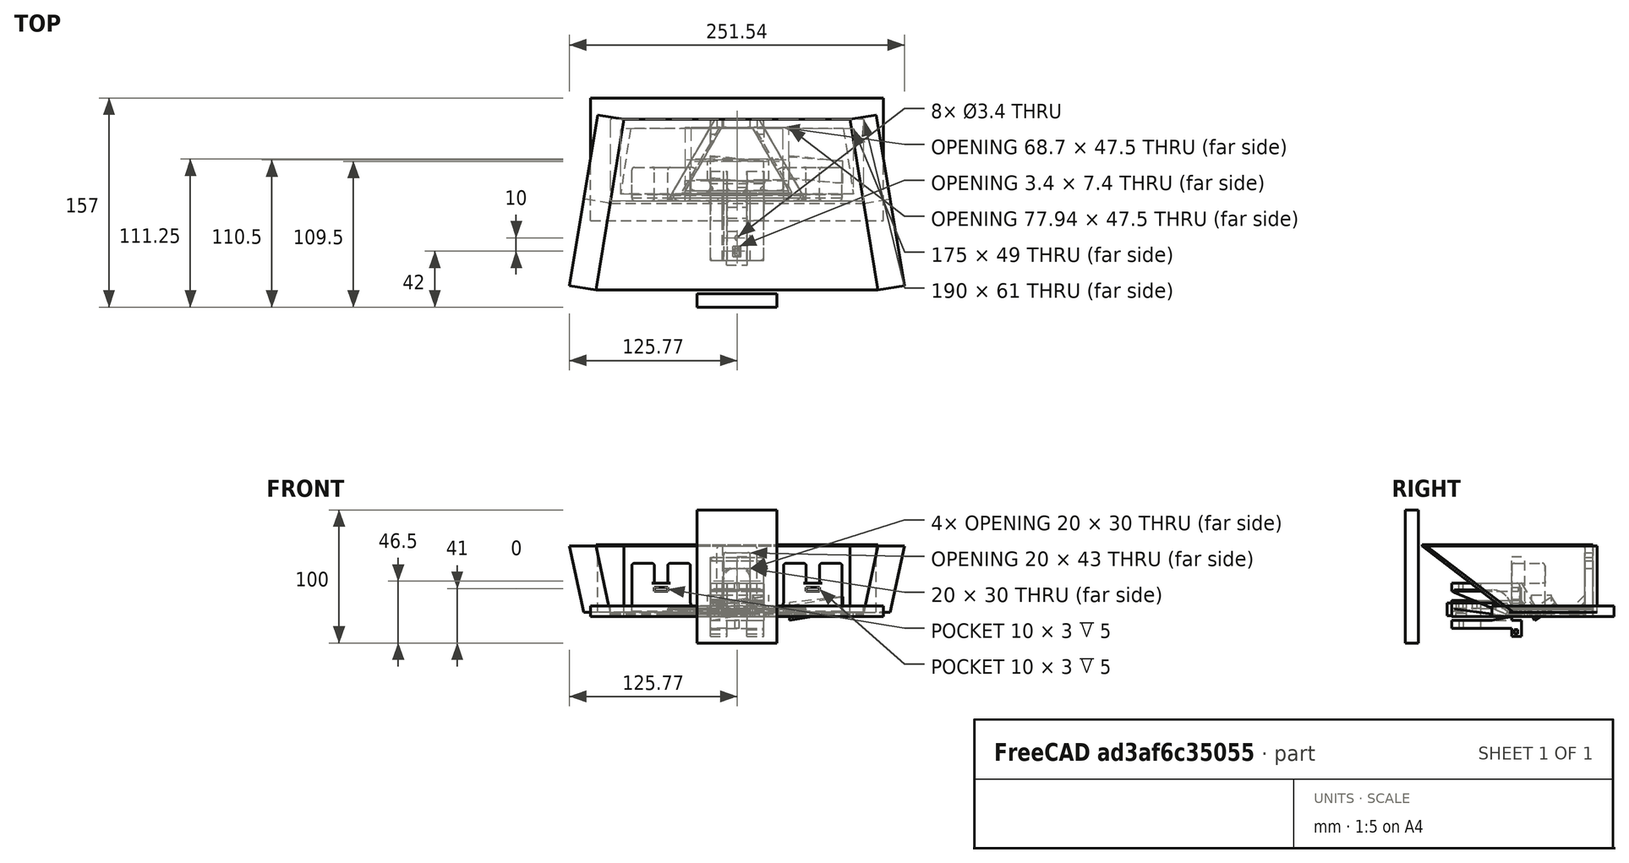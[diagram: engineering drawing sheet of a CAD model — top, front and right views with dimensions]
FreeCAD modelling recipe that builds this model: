
FCSTD DOCUMENT  (FreeCAD 1.0R39319 (Git))
Label: soporte_celular_auto_2bloques
License: All rights reserved
LicenseURL: http://en.wikipedia.org/wiki/All_rights_reserved
objects: Part::Box×64, Part::Cut×50, Part::Fillet×29, Part::Extrusion×19, Sketcher::SketchObject×18, Part::MultiFuse×16, Part::Feature×12, Part::Prism×6, Part::Cylinder×5, Part::Chamfer×2, Mesh::Feature×1
note: 239 computed .brp shape members not serialized (recipe doc carries the construction recipe); baked Part::Feature solids carry a one-line shape summary decoded from their .brp

FEATURE [Sketcher::SketchObject] Sketch001
  ArcFitTolerance = 0
  FullyConstrained = true
  MakeInternals = false
  sketch-geometry (4):
    g0: LineSegment StartX=-95 StartY=0 StartZ=0 EndX=95 EndY=-9e-16 EndZ=0
    g1: LineSegment StartX=-95 StartY=0 StartZ=0 EndX=-85 EndY=61 EndZ=0
    g2: LineSegment StartX=95 StartY=-9e-16 StartZ=0 EndX=85 EndY=61 EndZ=0
    g3: LineSegment StartX=-85 StartY=61 StartZ=0 EndX=85 EndY=61 EndZ=0
  constraints (10):
    c: PointOnObject(g0,g-1)
    c: Symmetric(g0,g0,g-2)
    c: DistanceX(g0,g0) = 190
    c: Coincident(g1,g0)
    c: Coincident(g2,g0)
    c: Coincident(g3,g1)
    c: Coincident(g3,g2)
    c: Symmetric(g1,g2,g-2)
    c: DistanceX(g3,g3) = 170
    c: DistanceY(g0,g2) = 61
FEATURE [Part::Extrusion] Extrude
  Base = -> Sketch001
  Dir = (0,0,1)
  DirMode = 2
  FaceMakerClass = Part::FaceMakerBullseye
  FaceMakerMode = 3
  LengthFwd = 10
  LengthRev = 0
  Solid = true
  Symmetric = false
FEATURE [Part::Box] Box  label="Cube"
  AttacherType = Attacher::AttachEngine3D
  Height = 8
  Length = 220
  Placement = pos=(-110,-15,0) rot=(0,0,1;0rad)
  Width = 92
FEATURE [Part::Cut] Cut  label="molde_cortador"
  Base = -> Box
  Tool = -> Extrude
FEATURE [Part::Prism] Prism002
  AttacherType = Attacher::AttachEngine3D
  Circumradius = 60
  FirstAngle = 0
  Height = 6
  Placement = pos=(0,23,0) rot=(0,0,-1;0.523599rad)
  Polygon = 3
  SecondAngle = 0
FEATURE [Part::Prism] Prism003
  AttacherType = Attacher::AttachEngine3D
  Circumradius = 45
  FirstAngle = 0
  Height = 6
  Placement = pos=(0,23,0) rot=(0,0,-1;0.523599rad)
  Polygon = 3
  SecondAngle = 0
FEATURE [Part::Cut] Cut001
  Base = -> Prism002
  Placement = pos=(0,7,0) rot=(0,0,1;0rad)
  Tool = -> Prism003
FEATURE [Part::Box] Box001  label="Cube001"
  AttacherType = Attacher::AttachEngine3D
  Height = 6
  Length = 32
  Placement = pos=(-16,55,0) rot=(0,0,1;0rad)
  Width = 6
FEATURE [Part::MultiFuse] Fusion
  Shapes = -> [Cut001,Box001]
FEATURE [Sketcher::SketchObject] Sketch002
  ArcFitTolerance = 0
  FullyConstrained = true
  MakeInternals = false
  sketch-geometry (4):
    g0: LineSegment StartX=-95 StartY=0 StartZ=0 EndX=95 EndY=-9e-16 EndZ=0
    g1: LineSegment StartX=-95 StartY=0 StartZ=0 EndX=-85 EndY=61 EndZ=0
    g2: LineSegment StartX=95 StartY=-9e-16 StartZ=0 EndX=85 EndY=61 EndZ=0
    g3: LineSegment StartX=-85 StartY=61 StartZ=0 EndX=85 EndY=61 EndZ=0
  constraints (10):
    c: PointOnObject(g0,g-1)
    c: Symmetric(g0,g0,g-2)
    c: DistanceX(g0,g0) = 190
    c: Coincident(g1,g0)
    c: Coincident(g2,g0)
    c: Coincident(g3,g1)
    c: Coincident(g3,g2)
    c: Symmetric(g1,g2,g-2)
    c: DistanceX(g3,g3) = 170
    c: DistanceY(g0,g2) = 61
FEATURE [Part::Box] Box002  label="Cube002"
  AttacherType = Attacher::AttachEngine3D
  Height = 8
  Length = 220
  Placement = pos=(-110,-15,0) rot=(0,0,1;0rad)
  Width = 113
FEATURE [Part::Extrusion] Extrude001
  Base = -> Sketch002
  Dir = (0,0,1)
  DirMode = 2
  FaceMakerClass = Part::FaceMakerBullseye
  FaceMakerMode = 3
  LengthFwd = 10
  LengthRev = 0
  Solid = true
  Symmetric = false
FEATURE [Part::Cut] Cut002  label="molde_cortador001"
  Base = -> Box002
  Tool = -> Extrude001
FEATURE [Part::Cut] Cut003  label="base_triangulo"
  Base = -> Fusion
  Tool = -> Cut002
FEATURE [Part::Box] Box003  label="Cube003"
  AttacherType = Attacher::AttachEngine3D
  Height = 3
  Length = 220
  Placement = pos=(-110,2,0) rot=(0,0,1;0rad)
  Width = 2.5
FEATURE [Part::Cut] Cut004  label="base_triangulo_con_canaleta"
  Base = -> Cut003
  Tool = -> Box003
FEATURE [Part::Feature] Fusion001
  shape: bbox 190 x 63 x 3 mm, 10 faces (baked)
FEATURE [Sketcher::SketchObject] Sketch003
  ArcFitTolerance = 0
  ExternalGeometry = -> [Fusion001]
  FullyConstrained = true
  MakeInternals = false
  sketch-geometry (4):
    g0: LineSegment StartX=-87.5 StartY=0 StartZ=0 EndX=87.5 EndY=0 EndZ=0
    g1: LineSegment StartX=-87.5 StartY=0 StartZ=0 EndX=-80 EndY=49 EndZ=0
    g2: LineSegment StartX=87.5 StartY=0 StartZ=0 EndX=80 EndY=49 EndZ=0
    g3: LineSegment StartX=-80 StartY=49 StartZ=0 EndX=80 EndY=49 EndZ=0
  constraints (10):
    c: PointOnObject(g0,g-1)
    c: Symmetric(g0,g0,g-2)
    c: DistanceX(g0,g0) = 175
    c: Coincident(g1,g0)
    c: Coincident(g2,g0)
    c: Coincident(g3,g1)
    c: Coincident(g3,g2)
    c: Symmetric(g1,g2,g-2)
    c: DistanceX(g3,g3) = 160
    c: DistanceY(g0,g2) = 49
FEATURE [Part::Extrusion] Extrude002
  Base = -> Sketch003
  Dir = (0,0,1)
  DirMode = 2
  FaceMakerClass = Part::FaceMakerBullseye
  FaceMakerMode = 3
  LengthFwd = 10
  LengthRev = 0
  Placement = pos=(0,5,0) rot=(0,0,1;0rad)
  Solid = true
  Symmetric = false
FEATURE [Part::Cut] Cut004002  label="base"
  Base = -> Fusion001
  Tool = -> Extrude002
FEATURE [Sketcher::SketchObject] Sketch004
  ArcFitTolerance = 0
  AttachmentSupport = -> [Cut004002]
  ExternalGeometry = -> [Cut004002]
  FullyConstrained = true
  MakeInternals = false
  MapMode = 5
  Placement = pos=(-92.5137,15.1662,-3.7e-15) rot=(-0.51489,0.606172,0.606172;4.09257rad)
  sketch-geometry (4):
    g0: LineSegment StartX=-46.4456 StartY=3 StartZ=0 EndX=17.3423 EndY=3 EndZ=0
    g1: LineSegment StartX=-46.4456 StartY=3 StartZ=0 EndX=-46.4456 EndY=53 EndZ=0
    g2: LineSegment StartX=-46.4456 StartY=53 StartZ=0 EndX=83.5544 EndY=53 EndZ=0
    g3: LineSegment StartX=83.5544 StartY=53 StartZ=0 EndX=17.3423 EndY=3 EndZ=0
  constraints (10):
    c: Coincident(g0,g-4)
    c: Coincident(g0,g-3)
    c: Vertical(g1)
    c: Coincident(g0,g1)
    c: DistanceY(g1,g1) = 50
    c: Coincident(g2,g1)
    c: Horizontal(g2)
    c: DistanceX(g2,g2) = 130
    c: Coincident(g3,g2)
    c: Coincident(g3,g0)
FEATURE [Part::Feature] Fusion002
  shape: bbox 190 x 63 x 3 mm, 10 faces (baked)
FEATURE [Sketcher::SketchObject] Sketch005
  ArcFitTolerance = 0
  ExternalGeometry = -> [Fusion002]
  FullyConstrained = true
  MakeInternals = false
  sketch-geometry (4):
    g0: LineSegment StartX=-87.5 StartY=0 StartZ=0 EndX=87.5 EndY=0 EndZ=0
    g1: LineSegment StartX=-87.5 StartY=0 StartZ=0 EndX=-80 EndY=49 EndZ=0
    g2: LineSegment StartX=87.5 StartY=0 StartZ=0 EndX=80 EndY=49 EndZ=0
    g3: LineSegment StartX=-80 StartY=49 StartZ=0 EndX=80 EndY=49 EndZ=0
  constraints (10):
    c: PointOnObject(g0,g-1)
    c: Symmetric(g0,g0,g-2)
    c: DistanceX(g0,g0) = 175
    c: Coincident(g1,g0)
    c: Coincident(g2,g0)
    c: Coincident(g3,g1)
    c: Coincident(g3,g2)
    c: Symmetric(g1,g2,g-2)
    c: DistanceX(g3,g3) = 160
    c: DistanceY(g0,g2) = 49
FEATURE [Part::Extrusion] Extrude003
  Base = -> Sketch005
  Dir = (0,0,1)
  DirMode = 2
  FaceMakerClass = Part::FaceMakerBullseye
  FaceMakerMode = 3
  LengthFwd = 10
  LengthRev = 0
  Placement = pos=(0,5,0) rot=(0,0,1;0rad)
  Solid = true
  Symmetric = false
FEATURE [Part::Cut] Cut004003  label="base001"
  Base = -> Fusion002
  Tool = -> Extrude003
FEATURE [Sketcher::SketchObject] Sketch006
  ArcFitTolerance = 0
  AttachmentSupport = -> [Cut004003]
  ExternalGeometry = -> [Cut004003]
  FullyConstrained = true
  MakeInternals = false
  MapMode = 5
  Placement = pos=(92.5137,15.1662,-2.34e-14) rot=(0.51489,0.606172,0.606172;2.19062rad)
  sketch-geometry (4):
    g0: LineSegment StartX=-17.3423 StartY=3 StartZ=0 EndX=46.4456 EndY=3 EndZ=0
    g1: LineSegment StartX=46.4456 StartY=3 StartZ=0 EndX=46.4456 EndY=53 EndZ=0
    g2: LineSegment StartX=46.4456 StartY=53 StartZ=0 EndX=-83.5544 EndY=53 EndZ=0
    g3: LineSegment StartX=-83.5544 StartY=53 StartZ=0 EndX=-17.3423 EndY=3 EndZ=0
  constraints (10):
    c: Coincident(g0,g-4)
    c: Coincident(g0,g-3)
    c: Coincident(g1,g0)
    c: Vertical(g1)
    c: DistanceY(g1,g1) = 50
    c: Coincident(g2,g1)
    c: Horizontal(g2)
    c: Coincident(g3,g2)
    c: DistanceX(g2,g2) = 130
    c: Coincident(g0,g3)
FEATURE [Part::Extrusion] Extrude004
  Base = -> Sketch006
  Dir = (0.986828,0.161775,1e-16)
  DirMode = 2
  FaceMakerClass = Part::FaceMakerBullseye
  FaceMakerMode = 3
  LengthFwd = 20
  LengthRev = 0
  Solid = true
  Symmetric = false
FEATURE [Part::Extrusion] Extrude006
  Base = -> Sketch004
  Dir = (-0.986828,0.161775,1e-16)
  DirMode = 2
  FaceMakerClass = Part::FaceMakerBullseye
  FaceMakerMode = 3
  LengthFwd = 20
  LengthRev = 0
  Solid = true
  Symmetric = false
FEATURE [Sketcher::SketchObject] Sketch
  ArcFitTolerance = 0
  ExternalGeometry = -> [Extrude006,Extrude004]
  FullyConstrained = true
  MakeInternals = false
  sketch-geometry (4):
    g0: LineSegment StartX=-85 StartY=61 StartZ=0 EndX=85 EndY=61 EndZ=0
    g1: LineSegment StartX=-106.031 StartY=-67.2876 StartZ=0 EndX=106.031 EndY=-67.2876 EndZ=0
    g2: LineSegment StartX=-85 StartY=61 StartZ=0 EndX=-106.031 EndY=-67.2876 EndZ=0
    g3: LineSegment StartX=85 StartY=61 StartZ=0 EndX=106.031 EndY=-67.2876 EndZ=0
  constraints (8):
    c: Coincident(g0,g-3)
    c: Coincident(g0,g-4)
    c: Coincident(g1,g-3)
    c: Coincident(g1,g-4)
    c: Coincident(g0,g2)
    c: Coincident(g0,g3)
    c: Coincident(g1,g2)
    c: Coincident(g1,g3)
FEATURE [Part::Extrusion] Extrude007  label="techo_posicion"
  Base = -> Sketch
  Dir = (0,0,1)
  DirMode = 2
  FaceMakerClass = Part::FaceMakerBullseye
  FaceMakerMode = 3
  LengthFwd = 1
  LengthRev = 0
  Placement = pos=(0,0,53) rot=(0,0,1;0rad)
  Solid = true
  Symmetric = false
FEATURE [Part::Box] Box004  label="Cube004"
  AttacherType = Attacher::AttachEngine3D
  Height = 44.5
  Length = 40
  Placement = pos=(-20,55,0) rot=(0,0,1;0rad)
  Width = 6
FEATURE [Part::Box] Box005  label="Cube005"
  AttacherType = Attacher::AttachEngine3D
  Height = 30
  Length = 20
  Placement = pos=(-10,55,6) rot=(0,0,1;0rad)
  Width = 6
FEATURE [Part::Cut] Cut004004  label="parte_trasera"
  Base = -> Box004
  Tool = -> Box005
FEATURE [Part::Box] Box006  label="Cube006"
  AttacherType = Attacher::AttachEngine3D
  Height = 6
  Length = 40
  Placement = pos=(0,0,20) rot=(0,0,1;0rad)
  Width = 51
FEATURE [Part::Box] Box007  label="Cube007"
  AttacherType = Attacher::AttachEngine3D
  Height = 6
  Length = 15
  Placement = pos=(12.5,22,20) rot=(0,0,1;0rad)
  Width = 70
FEATURE [Part::Cut] Cut004005
  Base = -> Box006
  Placement = pos=(-20,0,-1) rot=(0,0,1;0rad)
  Tool = -> Box007
FEATURE [Part::Cylinder] Cylinder
  Angle = 360
  AttacherType = Attacher::AttachEngine3D
  FirstAngle = 0
  Height = 30
  Placement = pos=(0,7,0) rot=(0,0,1;0rad)
  Radius = 1.7
  SecondAngle = 0
FEATURE [Part::Cut] Cut004006
  Base = -> Cut004005
  Placement = pos=(0,-45,0) rot=(0,0,1;0rad)
  Tool = -> Cylinder
FEATURE [Part::Box] Box008  label="celular"
  AttacherType = Attacher::AttachEngine3D
  Height = 100
  Length = 60
  Placement = pos=(-30,-80,-20) rot=(0,0,1;0rad)
  Width = 10
FEATURE [Part::Box] Box009  label="Cube008"
  AttacherType = Attacher::AttachEngine3D
  Height = 12
  Length = 12.5
  Placement = pos=(7.5,0,13) rot=(0,0,1;0rad)
  Width = 7.5
FEATURE [Part::Box] Box010  label="Cube009"
  AttacherType = Attacher::AttachEngine3D
  Height = 12
  Length = 12.5
  Placement = pos=(-20,0,13) rot=(0,0,1;0rad)
  Width = 7.5
FEATURE [Part::Feature] Fusion004001  label="Fusion005"
  shape: bbox 99.53 x 106 x 53 mm, 44 faces (baked)
FEATURE [Part::Fillet] Fillet006
  Base = -> Fusion004001
  EdgeLinks = -> Fusion004001 [Edge75,Edge79]
  Edges = 2 edges r=15: [Edge75,Edge79]
FEATURE [Part::Fillet] Fillet007
  Base = -> Fillet006
  EdgeLinks = -> Fillet006 [Edge65,Edge67]
  Edges = 2 edges r=2: [Edge65,Edge67]
FEATURE [Part::Fillet] Fillet008  label="soporte_final_v2.1_00"
  Base = -> Fillet007
  EdgeLinks = -> Fillet007 [Edge3,Edge19]
  Edges = 2 edges r=2: [Edge3,Edge19]
FEATURE [Part::Feature] Fillet008001  label="soporte_final_v2.002"
  shape: bbox 99.53 x 106 x 53 mm, 50 faces (baked)
FEATURE [Part::Box] Box011  label="Cube010"
  AttacherType = Attacher::AttachEngine3D
  Height = 100
  Length = 70
  Placement = pos=(10,-51,0) rot=(0,0,1;0rad)
  Width = 120
FEATURE [Part::Cut] Cut004007
  Base = -> Fillet008001
  Tool = -> Box011
FEATURE [Part::Box] Box012  label="Cube011"
  AttacherType = Attacher::AttachEngine3D
  Height = 100
  Length = 70
  Placement = pos=(-11,13,0) rot=(0,0,1;0rad)
  Width = 120
FEATURE [Part::Cut] Cut004008
  Base = -> Cut004007
  Tool = -> Box012
FEATURE [Part::Box] Box013  label="Cube012"
  AttacherType = Attacher::AttachEngine3D
  Height = 10
  Length = 40
  Placement = pos=(-60,0,2) rot=(0,0,1;0rad)
  Width = 70
FEATURE [Part::Cut] Cut004009
  Base = -> Cut004008
  Tool = -> Box013
FEATURE [Part::Box] Box014  label="Cube013"
  AttacherType = Attacher::AttachEngine3D
  Height = 50
  Length = 19
  Placement = pos=(-30,-60,0) rot=(0,0,1;0rad)
  Width = 60
FEATURE [Part::Cut] Cut004010
  Base = -> Cut004009
  Tool = -> Box014
FEATURE [Part::Box] Box015  label="Cube014"
  AttacherType = Attacher::AttachEngine3D
  Height = 30
  Length = 10
  Placement = pos=(-21,0,2) rot=(0,0,1;0rad)
  Width = 10
FEATURE [Part::Cut] Cut004011
  Base = -> Cut004010
  Tool = -> Box015
FEATURE [Part::Fillet] Fillet008002  label="soporte_final_v2.1"
  Base = -> Fillet008
  EdgeLinks = -> Fillet008 [Edge7,Edge53,Edge58,Edge60]
  Edges = 4 edges r=3: [Edge7,Edge53,Edge58,Edge60]
FEATURE [Part::Box] Box016  label="Cube015"
  AttacherType = Attacher::AttachEngine3D
  Height = 10
  Length = 40
  Placement = pos=(-54,-7,0) rot=(0,0,1;0rad)
  Width = 10
FEATURE [Part::Cut] Cut004012  label="test"
  Base = -> Cut004011
  Tool = -> Box016
FEATURE [Part::MultiFuse] Fusion004002  label="pieza_fronta_cuadrada_sin_soportes"
  Placement = pos=(0,0,-15) rot=(0,0,1;0rad)
  Shapes = -> [Cut004006,Box009,Box010]
FEATURE [Part::Box] Box017  label="Cube016"
  AttacherType = Attacher::AttachEngine3D
  Height = 22
  Length = 12.5
  Placement = pos=(7.5,0,3) rot=(0,0,1;0rad)
  Width = 7.5
FEATURE [Part::Cylinder] Cylinder001
  Angle = 360
  AttacherType = Attacher::AttachEngine3D
  FirstAngle = 0
  Height = 30
  Placement = pos=(0,7,0) rot=(0,0,1;0rad)
  Radius = 1.7
  SecondAngle = 0
FEATURE [Part::Box] Box018  label="Cube017"
  AttacherType = Attacher::AttachEngine3D
  Height = 6
  Length = 40
  Placement = pos=(0,0,20) rot=(0,0,1;0rad)
  Width = 51
FEATURE [Part::Box] Box019  label="Cube018"
  AttacherType = Attacher::AttachEngine3D
  Height = 6
  Length = 15
  Placement = pos=(12.5,22,20) rot=(0,0,1;0rad)
  Width = 70
FEATURE [Part::Cut] Cut004013
  Base = -> Box018
  Placement = pos=(-20,0,-1) rot=(0,0,1;0rad)
  Tool = -> Box019
FEATURE [Part::Cut] Cut004014
  Base = -> Cut004013
  Placement = pos=(0,-45,0) rot=(0,0,1;0rad)
  Tool = -> Cylinder001
FEATURE [Part::Box] Box020  label="Cube019"
  AttacherType = Attacher::AttachEngine3D
  Height = 22
  Length = 12.5
  Placement = pos=(-20,0,3) rot=(0,0,1;0rad)
  Width = 7.5
FEATURE [Part::MultiFuse] Fusion004004
  Shapes = -> [Cut004014,Box017,Box020]
FEATURE [Sketcher::SketchObject] Sketch009
  ArcFitTolerance = 0
  FullyConstrained = true
  MakeInternals = false
  sketch-geometry (4):
    g0: LineSegment StartX=-95 StartY=0 StartZ=0 EndX=95 EndY=-9e-16 EndZ=0
    g1: LineSegment StartX=-95 StartY=0 StartZ=0 EndX=-85 EndY=61 EndZ=0
    g2: LineSegment StartX=95 StartY=-9e-16 StartZ=0 EndX=85 EndY=61 EndZ=0
    g3: LineSegment StartX=-85 StartY=61 StartZ=0 EndX=85 EndY=61 EndZ=0
  constraints (10):
    c: PointOnObject(g0,g-1)
    c: Symmetric(g0,g0,g-2)
    c: DistanceX(g0,g0) = 190
    c: Coincident(g1,g0)
    c: Coincident(g2,g0)
    c: Coincident(g3,g1)
    c: Coincident(g3,g2)
    c: Symmetric(g1,g2,g-2)
    c: DistanceX(g3,g3) = 170
    c: DistanceY(g0,g2) = 61
FEATURE [Part::Extrusion] Extrude011
  Base = -> Sketch009
  Dir = (0,0,1)
  DirMode = 2
  FaceMakerClass = Part::FaceMakerBullseye
  FaceMakerMode = 3
  LengthFwd = 10
  LengthRev = 0
  Solid = true
  Symmetric = false
FEATURE [Part::Prism] Prism004
  AttacherType = Attacher::AttachEngine3D
  Circumradius = 45
  FirstAngle = 0
  Height = 6
  Placement = pos=(0,23,0) rot=(0,0,-1;0.523599rad)
  Polygon = 3
  SecondAngle = 0
FEATURE [Part::Box] Box023  label="corte_canaleta"
  AttacherType = Attacher::AttachEngine3D
  Height = 3
  Length = 220
  Placement = pos=(-110,2,0) rot=(0,0,1;0rad)
  Width = 2.5
FEATURE [Part::Box] Box024  label="Cube023"
  AttacherType = Attacher::AttachEngine3D
  Height = 8
  Length = 220
  Placement = pos=(-110,-15,0) rot=(0,0,1;0rad)
  Width = 113
FEATURE [Part::Cut] Cut004020  label="molde_cortador002"
  Base = -> Box024
  Tool = -> Extrude011
FEATURE [Part::Prism] Prism005
  AttacherType = Attacher::AttachEngine3D
  Circumradius = 60
  FirstAngle = 0
  Height = 6
  Placement = pos=(0,23,0) rot=(0,0,-1;0.523599rad)
  Polygon = 3
  SecondAngle = 0
FEATURE [Part::Cut] Cut004019
  Base = -> Prism005
  Placement = pos=(0,7,0) rot=(0,0,1;0rad)
  Tool = -> Prism004
FEATURE [Part::Box] Box026  label="Cube025"
  AttacherType = Attacher::AttachEngine3D
  Height = 6
  Length = 32
  Placement = pos=(-16,55,0) rot=(0,0,1;0rad)
  Width = 6
FEATURE [Part::MultiFuse] Fusion004005
  Shapes = -> [Cut004019,Box026]
FEATURE [Part::Cut] Cut004015  label="base_triangulo001"
  Base = -> Fusion004005
  Tool = -> Cut004020
FEATURE [Part::Cut] Cut004016  label="base_triangulo_con_canaleta001"
  Base = -> Cut004015
  Tool = -> Box023
FEATURE [Part::Feature] Fusion004009001  label="pieza_sin_refinar001"
  shape: bbox 103.9 x 106 x 42 mm, 40 faces (baked)
FEATURE [Part::Fillet] Fillet
  Base = -> Fusion004009001
  EdgeLinks = -> Fusion004009001 [Edge4,Edge8,Edge38,Edge44,Edge56,Edge57,Edge60,Edge62,Edge64,Edge66,Edge67,Edge68]
  Edges = 12 edges r=2: [Edge4,Edge8,Edge38,Edge44,Edge56,Edge57,Edge60,Edge62,Edge64,Edge66,Edge67,Edge68]
FEATURE [Part::Fillet] Fillet008003
  Base = -> Fillet
  EdgeLinks = -> Fillet [Edge92,Edge98]
  Edges = 2 edges r=2: [Edge92,Edge98]
FEATURE [Part::Fillet] Fillet008004
  Base = -> Fillet008003
  EdgeLinks = -> Fillet008003 [Edge22,Edge28,Edge83,Edge88]
  Edges = 4 edges r=2: [Edge22,Edge28,Edge83,Edge88]
FEATURE [Part::Fillet] Fillet008005
  Base = -> Fillet008004
  EdgeLinks = -> Fillet008004 [Edge105,Edge107,Edge108,Edge111]
  Edges = 4 edges r=5: [Edge105,Edge107,Edge108,Edge111]
FEATURE [Part::Fillet] Fillet008006
  Base = -> Fillet008005
  EdgeLinks = -> Fillet008005 [Edge107,Edge131]
  Edges = 2 edges r=1: [Edge107,Edge131]
FEATURE [Part::Fillet] Fillet008007
  Base = -> Fillet008006
  EdgeLinks = -> Fillet008006 [Edge3,Edge23]
  Edges = 2 edges r=2: [Edge3,Edge23]
FEATURE [Part::Chamfer] Chamfer  label="soporte_v2.2"
  Base = -> Fillet008007
  EdgeLinks = -> Fillet008007 [Edge154,Edge156]
  Edges = 2 edges r=5: [Edge154,Edge156]
FEATURE [Part::Box] Box028  label="Cube027"
  AttacherType = Attacher::AttachEngine3D
  Height = 113
  Length = 109
  Placement = pos=(-10,-55,0) rot=(0,0,1;0rad)
  Width = 156
FEATURE [Part::Feature] Chamfer001  label="soporte_v2.2_for_test"
  shape: bbox 101 x 106 x 42 mm, 68 faces (baked)
FEATURE [Part::Cut] Cut004021  label="test_v2.2"
  Base = -> Chamfer001
  Tool = -> Box028
FEATURE [Part::Box] Box029  label="refuerzo1"
  AttacherType = Attacher::AttachEngine3D
  Height = 6
  Length = 78
  Placement = pos=(-39,0,0) rot=(0,0,1;0rad)
  Width = 15
FEATURE [Part::Box] Box030  label="Cube029"
  AttacherType = Attacher::AttachEngine3D
  Height = 45
  Length = 10
  Width = 10
FEATURE [Part::Box] Box031  label="refuerzo2"
  AttacherType = Attacher::AttachEngine3D
  Height = 16
  Length = 46
  Placement = pos=(-22,15,0) rot=(0,0,1;0rad)
  Width = 15
FEATURE [Sketcher::SketchObject] Sketch010
  ArcFitTolerance = 0
  AttachmentSupport = -> [Fusion004002]
  ExternalGeometry = -> [Fusion004002,Box010]
  FullyConstrained = true
  MakeInternals = false
  MapMode = 5
  Placement = pos=(-20,0,-15) rot=(0.57735,-0.57735,-0.57735;2.0944rad)
  sketch-geometry (3):
    g0: LineSegment StartX=0 StartY=28 StartZ=0 EndX=0 EndY=19 EndZ=0
    g1: LineSegment StartX=0 StartY=19 StartZ=0 EndX=45 EndY=19 EndZ=0
    g2: LineSegment StartX=45 StartY=19 StartZ=0 EndX=0 EndY=28 EndZ=0
  constraints (6):
    c: Coincident(g0,g1)
    c: Coincident(g1,g2)
    c: Coincident(g0,g2)
    c: Coincident(g0,g-3)
    c: Coincident(g0,g-4)
    c: Coincident(g1,g-3)
FEATURE [Sketcher::SketchObject] Sketch011
  ArcFitTolerance = 0
  AttachmentSupport = -> [Box010]
  ExternalGeometry = -> [Box010]
  FullyConstrained = true
  MakeInternals = false
  MapMode = 5
  Placement = pos=(-20,0,13) rot=(0.57735,-0.57735,-0.57735;2.0944rad)
  sketch-geometry (3):
    g0: LineSegment StartX=-7.5 StartY=12 StartZ=0 EndX=-7.5 EndY=0 EndZ=0
    g1: LineSegment StartX=-7.5 StartY=0 StartZ=0 EndX=-15.5 EndY=0 EndZ=0
    g2: LineSegment StartX=-15.5 StartY=0 StartZ=0 EndX=-7.5 EndY=12 EndZ=0
  constraints (7):
    c: Horizontal(g1)
    c: DistanceX(g1,g1) = 8
    c: Coincident(g1,g0)
    c: Coincident(g0,g2)
    c: Coincident(g1,g2)
    c: Coincident(g0,g-3)
    c: Coincident(g-3,g0)
FEATURE [Part::Extrusion] Extrude012  label="soporte_trasero"
  Base = -> Sketch011
  Dir = (-1,0,0)
  DirMode = 2
  FaceMakerClass = Part::FaceMakerBullseye
  FaceMakerMode = 3
  LengthFwd = 12.5
  LengthRev = 0
  Placement = pos=(40,0,0) rot=(0,0,1;0rad)
  Solid = true
  Symmetric = false
FEATURE [Part::Extrusion] Extrude013  label="soporte_delantero"
  Base = -> Sketch010
  Dir = (-1,0,0)
  DirMode = 2
  FaceMakerClass = Part::FaceMakerBullseye
  FaceMakerMode = 3
  LengthFwd = 12.5
  LengthRev = 0
  Placement = pos=(40,0,0) rot=(0,0,1;0rad)
  Solid = true
  Symmetric = false
FEATURE [Part::Box] Box032  label="Cube030"
  AttacherType = Attacher::AttachEngine3D
  Height = 12
  Length = 12.5
  Placement = pos=(-20,0,13) rot=(0,0,1;0rad)
  Width = 7.5
FEATURE [Sketcher::SketchObject] Sketch012
  ArcFitTolerance = 0
  AttachmentSupport = -> [Box032]
  ExternalGeometry = -> [Box032]
  FullyConstrained = true
  MakeInternals = false
  MapMode = 5
  Placement = pos=(-20,0,13) rot=(0.57735,-0.57735,-0.57735;2.0944rad)
  sketch-geometry (3):
    g0: LineSegment StartX=-7.5 StartY=12 StartZ=0 EndX=-7.5 EndY=0 EndZ=0
    g1: LineSegment StartX=-7.5 StartY=0 StartZ=0 EndX=-15.5 EndY=0 EndZ=0
    g2: LineSegment StartX=-15.5 StartY=0 StartZ=0 EndX=-7.5 EndY=12 EndZ=0
  constraints (7):
    c: Horizontal(g1)
    c: DistanceX(g1,g1) = 8
    c: Coincident(g1,g0)
    c: Coincident(g0,g2)
    c: Coincident(g1,g2)
    c: Coincident(g0,g-3)
    c: Coincident(g-3,g0)
FEATURE [Part::Extrusion] Extrude014  label="soporte_trasero001"
  Base = -> Sketch012
  Dir = (-1,0,0)
  DirMode = 2
  FaceMakerClass = Part::FaceMakerBullseye
  FaceMakerMode = 3
  LengthFwd = 12.5
  LengthRev = 0
  Placement = pos=(12.5,0,0) rot=(0,0,1;0rad)
  Solid = true
  Symmetric = false
FEATURE [Sketcher::SketchObject] Sketch013
  ArcFitTolerance = 0
  FullyConstrained = false
  MakeInternals = false
  MapMode = 5
  Placement = pos=(-20,0,0) rot=(0.57735,-0.57735,-0.57735;2.0944rad)
  sketch-geometry (3):
    g0: LineSegment StartX=0 StartY=13 StartZ=0 EndX=0 EndY=19 EndZ=0
    g1: LineSegment StartX=0 StartY=19 StartZ=0 EndX=45 EndY=19 EndZ=0
    g2: LineSegment StartX=45 StartY=19 StartZ=0 EndX=0 EndY=13 EndZ=0
  constraints (3):
    c: Coincident(g0,g1)
    c: Coincident(g1,g2)
    c: Coincident(g0,g2)
FEATURE [Part::Extrusion] Extrude015  label="soporte_delantero001"
  Base = -> Sketch013
  Dir = (-1,0,0)
  DirMode = 2
  FaceMakerClass = Part::FaceMakerBullseye
  FaceMakerMode = 3
  LengthFwd = 12.5
  LengthRev = 0
  Placement = pos=(12.5,0,0) rot=(0,0,1;0rad)
  Solid = true
  Symmetric = false
FEATURE [Part::MultiFuse] Fusion004009003  label="pieza_frontal_cuadrada"
  Shapes = -> [Fusion004002,Extrude012,Extrude014,Extrude013,Extrude015]
FEATURE [Part::Box] Box033  label="corte_canaleta001"
  AttacherType = Attacher::AttachEngine3D
  Height = 3
  Length = 220
  Placement = pos=(-110,2,0) rot=(0,0,1;0rad)
  Width = 2.5
FEATURE [Part::Cut] Cut004022  label="pieza_frontal_cuadrada_canaleteada"
  Base = -> Fusion004009003
  Placement = pos=(0,0,-13) rot=(0,0,1;0rad)
  Tool = -> Box033
FEATURE [Sketcher::SketchObject] Sketch014
  ArcFitTolerance = 0
  AttachmentSupport = -> [Cut004022]
  ExternalGeometry = -> [Cut004022]
  FullyConstrained = true
  MakeInternals = false
  MapMode = 5
  Placement = pos=(0,16.7308,-1.84615) rot=(0,0.471858,0.881675;3.14159rad)
  sketch-geometry (3):
    g0: LineSegment StartX=-20 StartY=6.6564 StartZ=0 EndX=20 EndY=1.38675 EndZ=0
    g1: LineSegment StartX=20 StartY=1.38675 StartZ=0 EndX=20 EndY=-1.1094 EndZ=0
    g2: LineSegment StartX=20 StartY=-1.1094 StartZ=0 EndX=-20 EndY=6.6564 EndZ=0
  constraints (7):
    c: Coincident(g0,g1)
    c: Coincident(g1,g2)
    c: Coincident(g2,g0)
    c: Vertical(g1)
    c: DistanceY(g1,g-4) = 0
    c: Coincident(g0,g-3)
    c: Coincident(g0,g-5)
FEATURE [Part::Extrusion] Extrude016  label="reduerzo_frontal1"
  Base = -> Sketch014
  Dir = (0,0.83205,0.5547)
  DirMode = 2
  FaceMakerClass = Part::FaceMakerBullseye
  FaceMakerMode = 3
  LengthFwd = 20
  LengthRev = 0
  Solid = true
  Symmetric = false
FEATURE [Part::Extrusion] Extrude017  label="refuerzo_frontal2"
  Base = -> Sketch014
  Dir = (0,0.83205,0.5547)
  DirMode = 2
  FaceMakerClass = Part::FaceMakerBullseye
  FaceMakerMode = 3
  LengthFwd = 20
  LengthRev = 0
  Placement = pos=(59.5,0,0) rot=(0,0,1;0rad)
  Solid = true
  Symmetric = false
FEATURE [Part::MultiFuse] Fusion004009004  label="soporte_sin_refinar_v3"
  Shapes = -> [Cut004004,Cut004016,Cut004022,Extrude016,Extrude017]
FEATURE [Part::Feature] Fusion004009004001  label="soporte_sin_refinar_v004"
  shape: bbox 103.9 x 106 x 44.5 mm, 40 faces (baked)
FEATURE [Part::Fillet] Fillet008008
  Base = -> Fusion004009004001
  EdgeLinks = -> Fusion004009004001 [Edge110,Edge111,Edge112,Edge115]
  Edges = 4 edges r=5: [Edge110,Edge111,Edge112,Edge115]
FEATURE [Part::Fillet] Fillet008009
  Base = -> Fillet008008
  EdgeLinks = -> Fillet008008 [Edge54,Edge55]
  Edges = 2 edges r=5: [Edge54,Edge55]
FEATURE [Part::Fillet] Fillet008010
  Base = -> Fillet008009
  EdgeLinks = -> Fillet008009 [Edge8,Edge67]
  Edges = 2 edges r=3: [Edge8,Edge67]
FEATURE [Part::Fillet] Fillet008011
  Base = -> Fillet008010
  EdgeLinks = -> Fillet008010 [Edge66,Edge74]
  Edges = 2 edges r=5: [Edge66,Edge74]
FEATURE [Part::Fillet] Fillet008012
  Base = -> Fillet008011
  EdgeLinks = -> Fillet008011 [Edge70,Edge89]
  Edges = 2 edges r=5: [Edge70,Edge89]
FEATURE [Part::Fillet] Fillet008013
  Base = -> Fillet008012
  EdgeLinks = -> Fillet008012 [Edge8,Edge10,Edge12,Edge46,Edge50,Edge56]
  Edges = 6 edges r=3: [Edge8,Edge10,Edge12,Edge46,Edge50,Edge56]
FEATURE [Part::Fillet] Fillet008014
  Base = -> Fillet008013
  EdgeLinks = -> Fillet008013 [Edge64,Edge98,Edge144,Edge146,Edge153,Edge154]
  Edges = 6 edges r=3: [Edge64,Edge98,Edge144,Edge146,Edge153,Edge154]
FEATURE [Part::Fillet] Fillet008015
  Base = -> Fillet008014
  EdgeLinks = -> Fillet008014 [Edge154,Edge178]
  Edges = 2 edges r=2: [Edge154,Edge178]
FEATURE [Part::Fillet] Fillet008016
  Base = -> Fillet008015
  EdgeLinks = -> Fillet008015 [Edge143,Edge179]
  Edges = 2 edges r=2: [Edge143,Edge179]
FEATURE [Part::Fillet] Fillet008017  label="soporte_v3.1"
  Base = -> Fillet008016
  EdgeLinks = -> Fillet008016 [Edge110,Edge134]
  Edges = 2 edges r=3: [Edge110,Edge134]
FEATURE [Part::Cylinder] Cylinder002
  Angle = 360
  AttacherType = Attacher::AttachEngine3D
  FirstAngle = 0
  Height = 30
  Placement = pos=(0,-28,0) rot=(0,0,1;0rad)
  Radius = 1.7
  SecondAngle = 0
FEATURE [Part::Box] Box034  label="Cube031"
  AttacherType = Attacher::AttachEngine3D
  Height = 6
  Length = 15
  Placement = pos=(-7.5,-40,6) rot=(0,0,1;0rad)
  Width = 27
FEATURE [Part::Cut] Cut004023
  Base = -> Box034
  Tool = -> Cylinder002
FEATURE [Part::Cylinder] Cylinder003
  Angle = 360
  AttacherType = Attacher::AttachEngine3D
  FirstAngle = 0
  Height = 30
  Placement = pos=(0,-28,0) rot=(0,0,1;0rad)
  Radius = 1.7
  SecondAngle = 0
FEATURE [Part::Feature] Fillet008017001  label="soporte_v3.2"
  shape: bbox 96.6 x 106 x 44.5 mm, 78 faces (baked)
FEATURE [Part::Cut] Cut004024
  Base = -> Fillet008017001
  Tool = -> Cylinder003
FEATURE [Part::MultiFuse] Fusion004009004002
  Shapes = -> [Cut004024,Cut004023]
FEATURE [Part::Feature] Fusion004009004002001  label="soporte_3.2"
  shape: bbox 96.6 x 106 x 44.5 mm, 78 faces (baked)
FEATURE [Part::Box] Box035  label="Cube032"
  AttacherType = Attacher::AttachEngine3D
  Height = 10
  Length = 50
  Placement = pos=(-22,-1,-10) rot=(0,0,1;0rad)
  Width = 10
FEATURE [Part::Cut] Cut004025
  Base = -> Fusion004002
  Tool = -> Box035
FEATURE [Part::Box] Box036  label="corte_canaleta002"
  AttacherType = Attacher::AttachEngine3D
  Height = 3
  Length = 220
  Placement = pos=(-110,2,0) rot=(0,0,1;0rad)
  Width = 2.5
FEATURE [Part::Box] Box037  label="Cube033"
  AttacherType = Attacher::AttachEngine3D
  Height = 10
  Length = 30
  Placement = pos=(-14,0,0) rot=(0,0,1;0rad)
  Width = 7.5
FEATURE [Part::MultiFuse] Fusion004009004002002
  Shapes = -> [Cut004025,Box037]
FEATURE [Part::Cut] Cut004026
  Base = -> Fusion004009004002002
  Tool = -> Box036
FEATURE [Part::Box] Box038  label="Cube034"
  AttacherType = Attacher::AttachEngine3D
  Height = 10
  Length = 12.5
  Placement = pos=(-20,-45,0) rot=(0,0,1;0rad)
  Width = 46
FEATURE [Part::Box] Box039  label="Cube035"
  AttacherType = Attacher::AttachEngine3D
  Height = 10
  Length = 12.5
  Placement = pos=(7.5,-45,0) rot=(0,0,1;0rad)
  Width = 46
FEATURE [Sketcher::SketchObject] Sketch015
  ArcFitTolerance = 0
  AttachmentSupport = -> [Box038]
  ExternalGeometry = -> [Cut004026]
  FullyConstrained = true
  MakeInternals = false
  MapMode = 5
  Placement = pos=(-20,-45,0) rot=(0.57735,-0.57735,-0.57735;2.0944rad)
  sketch-geometry (3):
    g0: LineSegment StartX=-52.5 StartY=10 StartZ=0 EndX=-52.5 EndY=0 EndZ=0
    g1: LineSegment StartX=-52.5 StartY=0 StartZ=0 EndX=-57.5 EndY=0 EndZ=0
    g2: LineSegment StartX=-57.5 StartY=0 StartZ=0 EndX=-52.5 EndY=10 EndZ=0
  constraints (8):
    c: PointOnObject(g0,g-1)
    c: Vertical(g0)
    c: Coincident(g0,g1)
    c: PointOnObject(g1,g-1)
    c: Coincident(g1,g2)
    c: Coincident(g2,g0)
    c: DistanceX(g1,g1) = 5
    c: Coincident(g0,g-3)
FEATURE [Part::Extrusion] Extrude018
  Base = -> Sketch015
  Dir = (-1,0,0)
  DirMode = 2
  FaceMakerClass = Part::FaceMakerBullseye
  FaceMakerMode = 3
  LengthFwd = 40
  LengthRev = 0
  Placement = pos=(40,0,0) rot=(0,0,1;0rad)
  Solid = true
  Symmetric = false
FEATURE [Part::Box] Box040  label="Cube036"
  AttacherType = Attacher::AttachEngine3D
  Height = 10
  Length = 12.5
  Placement = pos=(-20,-45,0) rot=(0,0,1;0rad)
  Width = 46
FEATURE [Part::Box] Box041  label="Cube037"
  AttacherType = Attacher::AttachEngine3D
  Height = 6
  Length = 15
  Placement = pos=(12.5,22,20) rot=(0,0,1;0rad)
  Width = 70
FEATURE [Part::Box] Box042  label="Cube038"
  AttacherType = Attacher::AttachEngine3D
  Height = 12
  Length = 12.5
  Placement = pos=(7.5,0,13) rot=(0,0,1;0rad)
  Width = 7.5
FEATURE [Part::Cylinder] Cylinder004
  Angle = 360
  AttacherType = Attacher::AttachEngine3D
  FirstAngle = 0
  Height = 30
  Placement = pos=(0,7,0) rot=(0,0,1;0rad)
  Radius = 1.7
  SecondAngle = 0
FEATURE [Part::Box] Box043  label="Cube039"
  AttacherType = Attacher::AttachEngine3D
  Height = 12
  Length = 12.5
  Placement = pos=(-20,0,13) rot=(0,0,1;0rad)
  Width = 7.5
FEATURE [Part::Box] Box044  label="Cube040"
  AttacherType = Attacher::AttachEngine3D
  Height = 6
  Length = 40
  Placement = pos=(0,0,20) rot=(0,0,1;0rad)
  Width = 51
FEATURE [Part::Cut] Cut004028
  Base = -> Box044
  Placement = pos=(-20,0,-1) rot=(0,0,1;0rad)
  Tool = -> Box041
FEATURE [Part::Cut] Cut004027
  Base = -> Cut004028
  Placement = pos=(0,-45,0) rot=(0,0,1;0rad)
  Tool = -> Cylinder004
FEATURE [Part::MultiFuse] Fusion004009004002003  label="pieza_fronta_cuadrada_sin_soportes001"
  Placement = pos=(0,0,-15) rot=(0,0,1;0rad)
  Shapes = -> [Cut004027,Box042,Box043]
FEATURE [Part::Box] Box045  label="Cube041"
  AttacherType = Attacher::AttachEngine3D
  Height = 10
  Length = 30
  Placement = pos=(-14,0,0) rot=(0,0,1;0rad)
  Width = 7.5
FEATURE [Part::Box] Box046  label="corte_canaleta003"
  AttacherType = Attacher::AttachEngine3D
  Height = 3
  Length = 220
  Placement = pos=(-110,2,0) rot=(0,0,1;0rad)
  Width = 2.5
FEATURE [Part::Box] Box047  label="Cube042"
  AttacherType = Attacher::AttachEngine3D
  Height = 10
  Length = 50
  Placement = pos=(-22,-1,-10) rot=(0,0,1;0rad)
  Width = 10
FEATURE [Part::Cut] Cut004030
  Base = -> Fusion004009004002003
  Tool = -> Box047
FEATURE [Part::MultiFuse] Fusion004009004002004
  Shapes = -> [Cut004030,Box045]
FEATURE [Part::Cut] Cut004029
  Base = -> Fusion004009004002004
  Tool = -> Box046
FEATURE [Sketcher::SketchObject] Sketch016
  ArcFitTolerance = 0
  AttachmentSupport = -> [Box040]
  ExternalGeometry = -> [Cut004029]
  FullyConstrained = true
  MakeInternals = false
  MapMode = 5
  Placement = pos=(-20,-45,0) rot=(0.57735,-0.57735,-0.57735;2.0944rad)
  sketch-geometry (3):
    g0: LineSegment StartX=-52.5 StartY=10 StartZ=0 EndX=-52.5 EndY=0 EndZ=0
    g1: LineSegment StartX=-52.5 StartY=0 StartZ=0 EndX=-57.5 EndY=0 EndZ=0
    g2: LineSegment StartX=-57.5 StartY=0 StartZ=0 EndX=-52.5 EndY=10 EndZ=0
  constraints (8):
    c: PointOnObject(g0,g-1)
    c: Vertical(g0)
    c: Coincident(g0,g1)
    c: PointOnObject(g1,g-1)
    c: Coincident(g1,g2)
    c: Coincident(g2,g0)
    c: DistanceX(g1,g1) = 5
    c: Coincident(g0,g-3)
FEATURE [Part::Extrusion] Extrude019
  Base = -> Sketch016
  Dir = (-1,0,0)
  DirMode = 2
  FaceMakerClass = Part::FaceMakerBullseye
  FaceMakerMode = 3
  LengthFwd = 40
  LengthRev = 0
  Placement = pos=(-40,7.5,0) rot=(0,0,1;3.14159rad)
  Solid = true
  Symmetric = false
FEATURE [Part::MultiFuse] Fusion004009004002005  label="parte_frontal_v3.3_acanaletado"
  Shapes = -> [Cut004026,Box038,Cut004029,Extrude018,Box040,Box039,Extrude019]
FEATURE [Part::Box] Box048  label="Cube043"
  AttacherType = Attacher::AttachEngine3D
  Height = 30
  Length = 20
  Placement = pos=(-10,55,6) rot=(0,0,1;0rad)
  Width = 6
FEATURE [Part::Box] Box049  label="Cube044"
  AttacherType = Attacher::AttachEngine3D
  Height = 44.5
  Length = 40
  Placement = pos=(-20,55,0) rot=(0,0,1;0rad)
  Width = 6
FEATURE [Part::Cut] Cut004031  label="parte_trasera33"
  Base = -> Box049
  Tool = -> Box048
FEATURE [Sketcher::SketchObject] Sketch017
  ArcFitTolerance = 0
  FullyConstrained = true
  MakeInternals = false
  sketch-geometry (4):
    g0: LineSegment StartX=-95 StartY=0 StartZ=0 EndX=95 EndY=-9e-16 EndZ=0
    g1: LineSegment StartX=-95 StartY=0 StartZ=0 EndX=-85 EndY=61 EndZ=0
    g2: LineSegment StartX=95 StartY=-9e-16 StartZ=0 EndX=85 EndY=61 EndZ=0
    g3: LineSegment StartX=-85 StartY=61 StartZ=0 EndX=85 EndY=61 EndZ=0
  constraints (10):
    c: PointOnObject(g0,g-1)
    c: Symmetric(g0,g0,g-2)
    c: DistanceX(g0,g0) = 190
    c: Coincident(g1,g0)
    c: Coincident(g2,g0)
    c: Coincident(g3,g1)
    c: Coincident(g3,g2)
    c: Symmetric(g1,g2,g-2)
    c: DistanceX(g3,g3) = 170
    c: DistanceY(g0,g2) = 61
FEATURE [Part::Extrusion] Extrude020
  Base = -> Sketch017
  Dir = (0,0,1)
  DirMode = 2
  FaceMakerClass = Part::FaceMakerBullseye
  FaceMakerMode = 3
  LengthFwd = 10
  LengthRev = 0
  Solid = true
  Symmetric = false
FEATURE [Part::Prism] Prism006
  AttacherType = Attacher::AttachEngine3D
  Circumradius = 45
  FirstAngle = 0
  Height = 6
  Placement = pos=(0,23,0) rot=(0,0,-1;0.523599rad)
  Polygon = 3
  SecondAngle = 0
FEATURE [Part::Box] Box050  label="Cube045"
  AttacherType = Attacher::AttachEngine3D
  Height = 6
  Length = 32
  Placement = pos=(-16,55,0) rot=(0,0,1;0rad)
  Width = 6
FEATURE [Part::Box] Box051  label="corte_canaleta004"
  AttacherType = Attacher::AttachEngine3D
  Height = 3
  Length = 220
  Placement = pos=(-110,2,0) rot=(0,0,1;0rad)
  Width = 2.5
FEATURE [Part::Box] Box052  label="Cube046"
  AttacherType = Attacher::AttachEngine3D
  Height = 8
  Length = 220
  Placement = pos=(-110,-15,0) rot=(0,0,1;0rad)
  Width = 113
FEATURE [Part::Cut] Cut004035  label="molde_cortador003"
  Base = -> Box052
  Tool = -> Extrude020
FEATURE [Part::Prism] Prism007
  AttacherType = Attacher::AttachEngine3D
  Circumradius = 60
  FirstAngle = 0
  Height = 6
  Placement = pos=(0,23,0) rot=(0,0,-1;0.523599rad)
  Polygon = 3
  SecondAngle = 0
FEATURE [Part::Cut] Cut004032
  Base = -> Prism007
  Placement = pos=(0,7,0) rot=(0,0,1;0rad)
  Tool = -> Prism006
FEATURE [Part::MultiFuse] Fusion004009004002006
  Shapes = -> [Cut004032,Box050]
FEATURE [Part::Cut] Cut004034  label="base_triangulo002"
  Base = -> Fusion004009004002006
  Tool = -> Cut004035
FEATURE [Part::Cut] Cut004033  label="base_triangulo_con_canaleta33"
  Base = -> Cut004034
  Tool = -> Box051
FEATURE [Part::Feature] Fusion004009004002007001  label="soporte_3.3_sin_refinar001"
  shape: bbox 103.9 x 106 x 44.5 mm, 35 faces (baked)
FEATURE [Part::Box] Box053  label="Cube047"
  AttacherType = Attacher::AttachEngine3D
  Height = 10
  Length = 15
  Placement = pos=(-7.5,-45,0) rot=(0,0,1;0rad)
  Width = 22
FEATURE [Part::Box] Box054  label="Cube048"
  AttacherType = Attacher::AttachEngine3D
  Height = 9.5
  Length = 15.7
  Placement = pos=(-7.85,-48.45,0.5) rot=(0,0,1;0rad)
  Width = 3.45
FEATURE [Part::MultiFuse] Fusion004009004002007002
  Shapes = -> [Box053,Box054]
FEATURE [Sketcher::SketchObject] Sketch018
  ArcFitTolerance = 0
  AttachmentSupport = -> [Fusion004009004002007001]
  FullyConstrained = true
  MakeInternals = false
  MapMode = 5
  Placement = pos=(0,0,10) rot=(0,0,1;0rad)
  sketch-geometry (4):
    g0: ArcOfCircle CenterX=-1e-16 CenterY=-36 CenterZ=0 NormalX=0 NormalY=0 NormalZ=1 AngleXU=0 Radius=1.7 StartAngle=0 EndAngle=3.14159
    g1: ArcOfCircle CenterX=-1e-16 CenterY=-40 CenterZ=0 NormalX=0 NormalY=0 NormalZ=1 AngleXU=0 Radius=1.7 StartAngle=3.14159 EndAngle=6.28319
    g2: LineSegment StartX=-1.7 StartY=-36 StartZ=0 EndX=-1.7 EndY=-40 EndZ=0
    g3: LineSegment StartX=1.7 StartY=-36 StartZ=0 EndX=1.7 EndY=-40 EndZ=0
  constraints (10):
    c: Tangent(g0,g3) = 1.5708
    c: Tangent(g0,g2) = -1.5708
    c: Tangent(g2,g1) = -1.5708
    c: Tangent(g3,g1) = 1.5708
    c: Vertical(g2)
    c: Equal(g0,g1)
    c: DistanceX(g0,g0) = 3.4
    c: DistanceY(g1,g0) = 4
    c: DistanceX(g0,g-1) = 1.7
    c: DistanceY(g0,g-1) = 36
FEATURE [Part::Extrusion] Extrude021
  Base = -> Sketch018
  Dir = (0,0,1)
  DirMode = 2
  FaceMakerClass = Part::FaceMakerBullseye
  FaceMakerMode = 3
  LengthFwd = 12
  LengthRev = 0
  Placement = pos=(0,0,-11) rot=(0,0,1;0rad)
  Solid = true
  Symmetric = false
FEATURE [Part::Cut] Cut004036  label="refuerzo_parte_frontal_33_001"
  Base = -> Fusion004009004002007002
  Tool = -> Extrude021
FEATURE [Part::Feature] Fusion004009004002007003  label="soporte_3.3_sin_refinar002"
  shape: bbox 103.9 x 106 x 44.5 mm, 35 faces (baked)
FEATURE [Sketcher::SketchObject] Sketch019
  ArcFitTolerance = 0
  AttachmentSupport = -> [Fusion004009004002007003]
  FullyConstrained = true
  MakeInternals = false
  MapMode = 5
  Placement = pos=(0,0,10) rot=(0,0,1;0rad)
  sketch-geometry (4):
    g0: ArcOfCircle CenterX=-1e-16 CenterY=-36 CenterZ=0 NormalX=0 NormalY=0 NormalZ=1 AngleXU=0 Radius=1.7 StartAngle=0 EndAngle=3.14159
    g1: ArcOfCircle CenterX=-1e-16 CenterY=-40 CenterZ=0 NormalX=0 NormalY=0 NormalZ=1 AngleXU=0 Radius=1.7 StartAngle=3.14159 EndAngle=6.28319
    g2: LineSegment StartX=-1.7 StartY=-36 StartZ=0 EndX=-1.7 EndY=-40 EndZ=0
    g3: LineSegment StartX=1.7 StartY=-36 StartZ=0 EndX=1.7 EndY=-40 EndZ=0
  constraints (10):
    c: Tangent(g0,g3) = 1.5708
    c: Tangent(g0,g2) = -1.5708
    c: Tangent(g2,g1) = -1.5708
    c: Tangent(g3,g1) = 1.5708
    c: Vertical(g2)
    c: Equal(g0,g1)
    c: DistanceX(g0,g0) = 3.4
    c: DistanceY(g1,g0) = 4
    c: DistanceX(g0,g-1) = 1.7
    c: DistanceY(g0,g-1) = 36
FEATURE [Part::Extrusion] Extrude022
  Base = -> Sketch019
  Dir = (0,0,1)
  DirMode = 2
  FaceMakerClass = Part::FaceMakerBullseye
  FaceMakerMode = 3
  LengthFwd = 12
  LengthRev = 0
  Placement = pos=(0,0,-11) rot=(0,0,1;0rad)
  Solid = true
  Symmetric = false
FEATURE [Part::Cut] Cut004037  label="parte_fronrtal_33"
  Base = -> Fusion004009004002005
  Tool = -> Extrude022
FEATURE [Part::Box] Box055  label="Cube049"
  AttacherType = Attacher::AttachEngine3D
  Height = 2.5
  Length = 6.3
  Placement = pos=(-3.15,-42,0) rot=(0,0,1;0rad)
  Width = 8
FEATURE [Part::Cut] Cut004038  label="refuerzo_parte_frontal_34"
  Base = -> Cut004036
  Tool = -> Box055
FEATURE [Part::MultiFuse] Fusion004009004002007004  label="parte_frontal_con_refuerzo34"
  Shapes = -> [Cut004037,Cut004038]
FEATURE [Part::MultiFuse] Fusion004009004002007005  label="soporte_3.4_sin_refinar"
  Shapes = -> [Cut004031,Cut004033,Fusion004009004002007004]
FEATURE [Part::Feature] Fusion004009004002007005001  label="soporte_3.4"
  shape: bbox 103.9 x 109.5 x 44.5 mm, 46 faces (baked)
FEATURE [Part::Fillet] Fillet008017002
  Base = -> Fusion004009004002007005001
  EdgeLinks = -> Fusion004009004002007005001 [Edge94,Edge95,Edge96,Edge99]
  Edges = 4 edges r=8: [Edge94,Edge95,Edge96,Edge99]
FEATURE [Part::Chamfer] Chamfer002
  Base = -> Fillet008017002
  EdgeLinks = -> Fillet008017002 [Edge52,Edge53]
  Edges = 2 edges r=10: [Edge52,Edge53]
FEATURE [Part::Fillet] Fillet008017003
  Base = -> Chamfer002
  EdgeLinks = -> Chamfer002 [Edge60,Edge90]
  Edges = 2 edges r=5: [Edge60,Edge90]
FEATURE [Part::Fillet] Fillet008017004
  Base = -> Fillet008017003
  EdgeLinks = -> Fillet008017003 [Edge21,Edge67]
  Edges = 2 edges r=5: [Edge21,Edge67]
FEATURE [Part::Fillet] Fillet008017005
  Base = -> Fillet008017004
  EdgeLinks = -> Fillet008017004 [Edge30]
  Edges = 1 edges r=5: [Edge30]
FEATURE [Part::Fillet] Fillet008017006  label="soporte_3.4_final"
  Base = -> Fillet008017005
  EdgeLinks = -> Fillet008017005 [Edge7,Edge9,Edge74,Edge76]
  Edges = 4 edges r=2: [Edge7,Edge9,Edge74,Edge76]
FEATURE [Part::Box] Box056  label="Cube050"
  AttacherType = Attacher::AttachEngine3D
  Height = 25
  Length = 78
  Placement = pos=(-40,-78,-7) rot=(0,0,1;0rad)
  Width = 78
FEATURE [Part::Cut] Cut004039
  Base = -> Fillet008017006
  Tool = -> Box056
FEATURE [Part::Box] Box057  label="Cube051"
  AttacherType = Attacher::AttachEngine3D
  Height = 21
  Length = 50
  Placement = pos=(-25,7.5,0) rot=(0,0,1;0rad)
  Width = 11
FEATURE [Part::Cut] Cut004040
  Base = -> Cut004039
  Tool = -> Box057
FEATURE [Part::Box] Box058  label="Cube052"
  AttacherType = Attacher::AttachEngine3D
  Height = 10
  Length = 56
  Placement = pos=(-26,0,6) rot=(0,0,1;0rad)
  Width = 10
FEATURE [Part::Cut] Cut004041
  Base = -> Cut004040
  Tool = -> Box058
FEATURE [Part::Box] Box059  label="Cube053"
  AttacherType = Attacher::AttachEngine3D
  Height = 40
  Length = 44
  Placement = pos=(35,0,0) rot=(0,0,1;0rad)
  Width = 25
FEATURE [Part::Box] Box060  label="Cube054"
  AttacherType = Attacher::AttachEngine3D
  Height = 40
  Length = 44
  Placement = pos=(-79,0,0) rot=(0,0,1;0rad)
  Width = 25
FEATURE [Part::Box] Box061  label="Cube055"
  AttacherType = Attacher::AttachEngine3D
  Height = 10
  Length = 200
  Placement = pos=(-95,2,-6) rot=(0,0,1;0rad)
  Width = 2.5
FEATURE [Part::Box] Box064  label="Cube058"
  AttacherType = Attacher::AttachEngine3D
  Height = 15
  Length = 10
  Placement = pos=(-62,-8,25) rot=(0,0,1;0rad)
  Width = 50
FEATURE [Part::Box] Box065  label="Cube059"
  AttacherType = Attacher::AttachEngine3D
  Height = 15
  Length = 10
  Placement = pos=(52,-8,25) rot=(0,0,1;0rad)
  Width = 50
FEATURE [Part::Box] Box066  label="Cube060"
  AttacherType = Attacher::AttachEngine3D
  Height = 3
  Length = 10
  Placement = pos=(52,0,19) rot=(0,0,1;0rad)
  Width = 5
FEATURE [Part::Box] Box067  label="Cube061"
  AttacherType = Attacher::AttachEngine3D
  Height = 3
  Length = 10
  Placement = pos=(-62,0,19) rot=(0,0,1;0rad)
  Width = 5
FEATURE [Part::Box] Box068  label="Cube062"
  AttacherType = Attacher::AttachEngine3D
  Height = 3
  Length = 10
  Placement = pos=(52,28,19) rot=(0,0,1;0rad)
  Width = 5
FEATURE [Part::Box] Box069  label="Cube063"
  AttacherType = Attacher::AttachEngine3D
  Height = 3
  Length = 10
  Placement = pos=(-62,28,19) rot=(0,0,1;0rad)
  Width = 5
FEATURE [Part::MultiFuse] Fusion004009004002007005002
  Refine = true
  Shapes = -> [Cut004041,Box059,Box060]
FEATURE [Part::Cut] Cut004042
  Base = -> Fusion004009004002007005002
  Refine = true
  Tool = -> Box061
FEATURE [Part::Cut] Cut004043
  Base = -> Cut004042
  Refine = true
  Tool = -> Box064
FEATURE [Part::Cut] Cut004044
  Base = -> Cut004043
  Refine = true
  Tool = -> Box065
FEATURE [Part::Cut] Cut004045
  Base = -> Cut004044
  Refine = true
  Tool = -> Box069
FEATURE [Part::Cut] Cut004046
  Base = -> Cut004045
  Refine = true
  Tool = -> Box068
FEATURE [Part::Cut] Cut004047
  Base = -> Cut004046
  Refine = true
  Tool = -> Box067
FEATURE [Part::Cut] Cut004048
  Base = -> Cut004047
  Refine = true
  Tool = -> Box066
FEATURE [Part::Fillet] Fillet008017007
  Base = -> Cut004048
  EdgeLinks = -> Cut004048 [Edge43,Edge46,Edge94,Edge96]
  Edges = 4 edges r=5: [Edge43,Edge46,Edge94,Edge96]
FEATURE [Part::Fillet] Fillet008017008
  Base = -> Fillet008017007
  EdgeLinks = -> Fillet008017007 [Edge16,Edge17,Edge20,Edge21,Edge81,Edge82,Edge126,Edge127]
  Edges = 8 edges r=3: [Edge16,Edge17,Edge20,Edge21,Edge81,Edge82,Edge126,Edge127]
FEATURE [Part::Fillet] Fillet008017009
  Base = -> Fillet008017008
  EdgeLinks = -> Fillet008017008 [Edge46,Edge47,Edge48,Edge50,Edge52,Edge54,Edge56,Edge110,Edge111,Edge140,Edge141,Edge143,Edge146,Edge147,Edge148,Edge149,Edge163,Edge166]
  Edges = 18 edges r=2: [Edge46,Edge47,Edge48,Edge50,Edge52,Edge54,Edge56,Edge110,Edge111,Edge140,Edge141,Edge143,Edge146,Edge147,Edge148,Edge149,Edge163,Edge166]
FEATURE [Part::Fillet] Fillet008017010
  Base = -> Fillet008017009
  EdgeLinks = -> Fillet008017009 [Edge4,Edge6,Edge17,Edge20,Edge21,Edge22,Edge27,Edge31,Edge33,Edge34,Edge69,Edge72,Edge74,Edge76,Edge101,Edge102]
  Edges = 16 edges r=2: [Edge4,Edge6,Edge17,Edge20,Edge21,Edge22,Edge27,Edge31,Edge33,Edge34,Edge69,Edge72,Edge74,Edge76,Edge101,Edge102]
FEATURE [Mesh::Feature] Mesh  label="Fillet008017010 (Meshed)"
